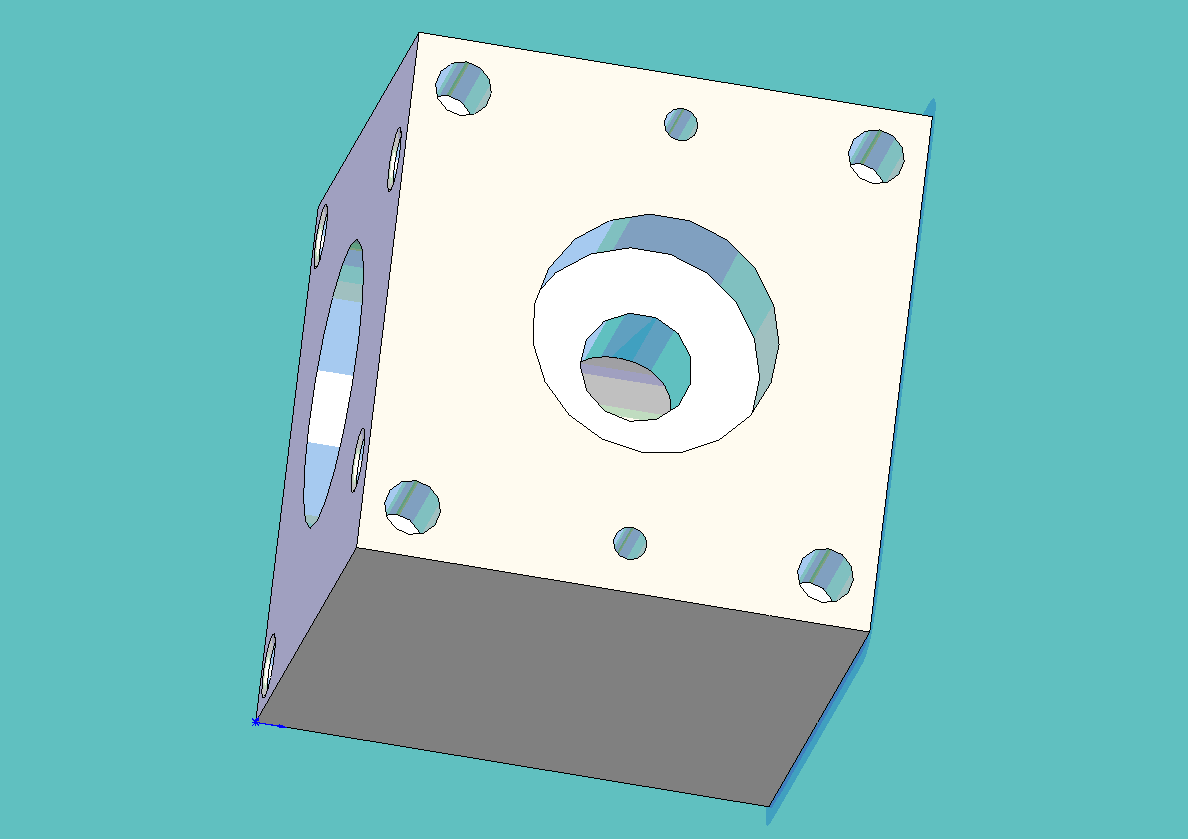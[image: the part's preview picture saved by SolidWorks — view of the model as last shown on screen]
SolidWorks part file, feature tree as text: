
SOLIDWORKS PART (.sldprt)
format: sldprt  version: not decoded by parser v0  size: 360,448 bytes
history: native  units: mm
features: sketch x8, cut_extrude x7, material x1, extrude x1, fillet x1 (+13 scaffold rows collapsed)
feature tree (31):
  scaffold x13  (default folders/planes/origin — collapsed)
  material  "7079 Alloy"
  sketch  "Sketch1"  dims[D1=82.55mm D2=~72.344581mm]
  extrude  "Extrude1"  Depth=73.025mm
  sketch  "Sketch2"  dims[D3=20.32mm D6=7.9375mm D1=~38.166241mm D2=~38.156504mm D4=6.35mm D5=6.35mm D7=6.3522mm D8=6.35mm D9=15.875mm D10=73.025mm D11=15.875mm]
  cut_extrude  "Cut-Extrude1"  Depth=73.025mm
  sketch  "Sketch3"  dims[D3=63.5mm D4=38.1mm D1=38.1mm D2=38.1mm]
  sketch  "Sketch5"
  cut_extrude  "Cut-Extrude2"  Depth=8.6741mm
  sketch  "Sketch6"  dims[D1=7.9375mm D2=34.925mm D3=15.875mm D4=15.875mm]
  cut_extrude  "Cut-Extrude3"  Depth=15.875mm
  fillet  "Fillet1"  Radius=0.635mm
  cut_extrude  "Cut-Extrude4"  Depth=0.635mm
  sketch  "Sketch7"  dims[c1.D4=34.925mm c1.D7=7.9375mm c1.D10=7.9375mm c1.D11=7.9375mm c1.D13=7.9375mm c1.D14=~0.237986mm c1.D16=4.7625mm c1.D17=4.7625mm c1.D19=4.7625mm c1.D1=34.925mm c1.D2=38.1mm c1.D3=38.1mm c1.D5=7.1374mm c1.D6=7.1374mm c1.D8=69.0626mm c1.D9=~65.887304mm c2.D10=~65.887304mm c2.D12=7.1374mm c2.D14=7.1374mm c2.D15=34.925mm c2.D18=34.925mm c2.D19=7.1374mm c2.D20=~65.887304mm c2.D21=7.1374mm c2.D22=69.0626mm]
  cut_extrude  "Cut-Extrude5"  Depth=15.875mm
  sketch  "Sketch8"  dims[D1=15.875mm D2=34.925mm D3=38.1mm]
  cut_extrude  "Cut-Extrude6"  Depth=50.8mm
  sketch  "Sketch9"  dims[D1=22.225mm]
  cut_extrude  "Cut-Extrude7"  Depth=57.15mm
decode coverage: 16 of 17 modeling features carry decoded parameters
note: ~ marks probable driven/reference dimensions
note: suppression state not decoded; provenance and decode notes live in map.json
